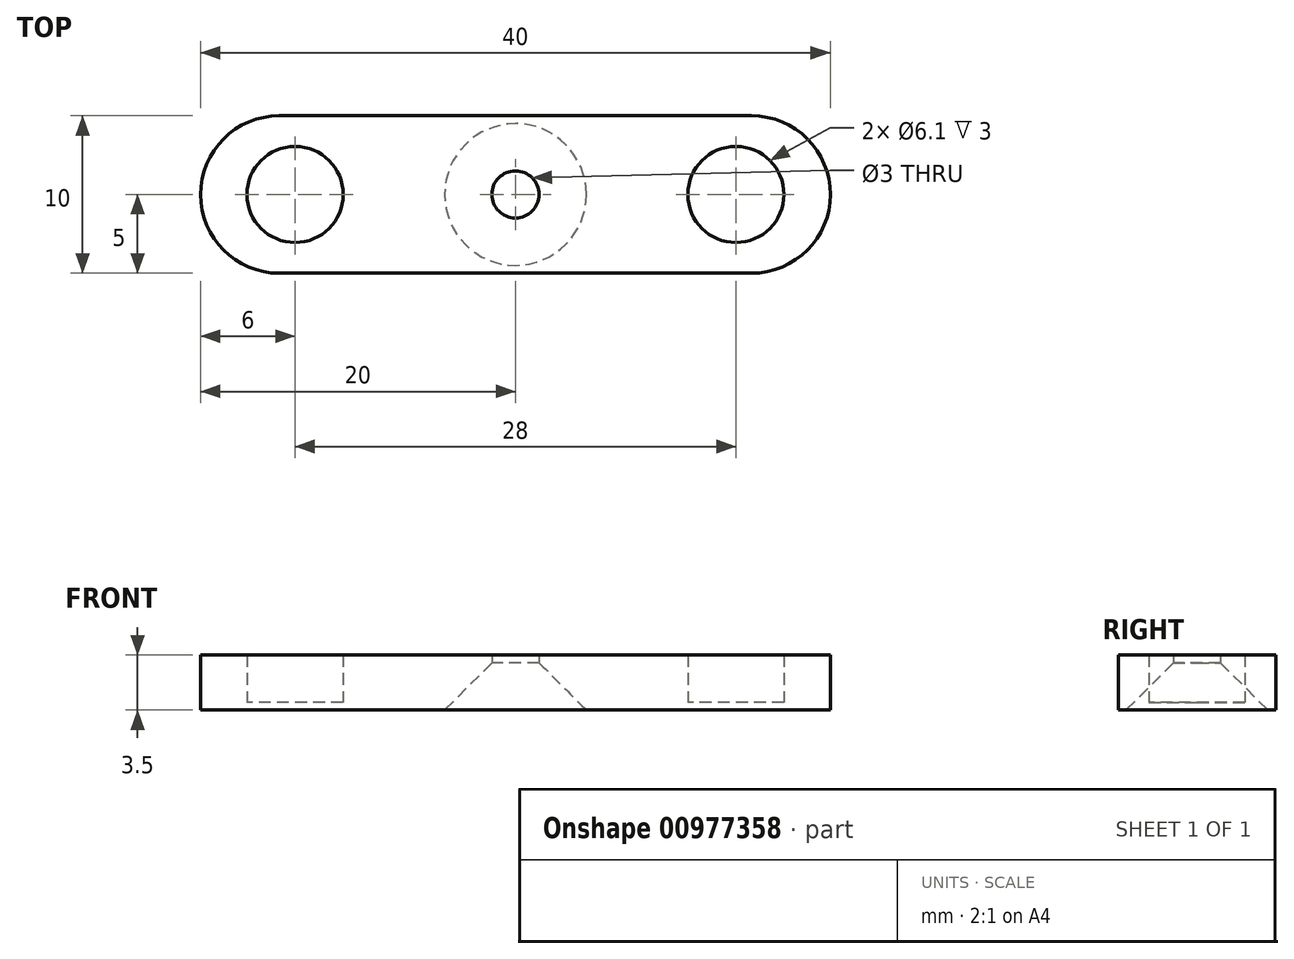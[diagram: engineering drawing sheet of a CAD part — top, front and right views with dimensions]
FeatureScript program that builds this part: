
annotation { "Feature Type Name" : "Feature", "Feature Type Description" : "" }
export const myFeature = defineFeature(function(context is Context, id is Id, definition is map)
    precondition{}
    {
        {
            var Q0;
            Q0=qCreatedBy(makeId("Top.planeOp"),FACE);
            var sketch = newSketch(context, id + "F0", { "sketchPlane" : qUnion([Q0])});
            skLineSegment(sketch, "E0.bottom", {"start": v(20, 5) * mm, "end": v(-20, 5) * mm});
            skLineSegment(sketch, "E0.top", {"start": v(20, -5) * mm, "end": v(-20, -5) * mm});
            skLineSegment(sketch, "E0.left", {"start": v(20, 5) * mm, "end": v(20, -5) * mm});
            skLineSegment(sketch, "E0.right", {"start": v(-20, 5) * mm, "end": v(-20, -5) * mm});
            skPoint(sketch, "E0.middle", {"position": v(0, 0) * mm});
            skCircle(sketch, "E1", {"center": v(-14, 0) * mm, "radius": 3.05 * mm});
            skCircle(sketch, "E2", {"center": v(14, 0) * mm, "radius": 3.05 * mm});
            skCircle(sketch, "E3", {"center": v(0, 0) * mm, "radius": 1.5 * mm});
            skSolve(sketch);
        }
        {
            var Q0;
            Q0=makeQuery(id+"F0.imprint","IMPRINT",FACE,{"disambiguationData":[TD([[makeQuery(id+"F0.imprint","IMPRINT",EDGE,{"derivedFrom":sQuery(id+"F0.wireOp",EDGE,"E0.bottom")}),1.0]])]});
            var Q1;
            Q1=makeQuery(id+"F0.imprint","IMPRINT",FACE,{"disambiguationData":[TD([[makeQuery(id+"F0.imprint","IMPRINT",EDGE,{"derivedFrom":sQuery(id+"F0.wireOp",EDGE,"E1")}),1.0]])]});
            var Q2;
            Q2=makeQuery(id+"F0.imprint","IMPRINT",FACE,{"disambiguationData":[TD([[makeQuery(id+"F0.imprint","IMPRINT",EDGE,{"derivedFrom":sQuery(id+"F0.wireOp",EDGE,"E2")}),1.0]])]});
            extrude(context, id + "F1", {"entities" : qUnion([Q0, Q1, Q2]), "depth" : 0.5 * mm, "offsetDistance" : 25 * mm});
        }
        {
            var Q0;
            Q0=makeQuery(id+"F0.imprint","IMPRINT",FACE,{"disambiguationData":[TD([[makeQuery(id+"F0.imprint","IMPRINT",EDGE,{"derivedFrom":sQuery(id+"F0.wireOp",EDGE,"E0.bottom")}),1.0]])]});
            extrude(context, id + "F2", {"entities" : qUnion([Q0]), "operationType" : NewBodyOperationType.ADD, "depth" : 3.5 * mm, "offsetDistance" : 25 * mm});
        }
        {
            var Q0;
            {var subQ0=sQuery(id+"F0.wireOp",EDGE,"E0.left");var subQ1=sQuery(id+"F0.wireOp",EDGE,"E0.bottom");Q0=makeQuery(id+"F2.boolean.opBoolean","MERGE",EDGE,{"derivedFrom":[makeQuery(id+"F1.opExtrude","SWEPT_EDGE",EDGE,{"disambiguationData":[OSD([subQ1,subQ0])]}),makeQuery(id+"F2.opExtrude","SWEPT_EDGE",EDGE,{"disambiguationData":[OSD([subQ1,subQ0])]})]});}
            var Q1;
            {var subQ0=sQuery(id+"F0.wireOp",EDGE,"E0.left");var subQ1=sQuery(id+"F0.wireOp",EDGE,"E0.top");Q1=makeQuery(id+"F2.boolean.opBoolean","MERGE",EDGE,{"derivedFrom":[makeQuery(id+"F1.opExtrude","SWEPT_EDGE",EDGE,{"disambiguationData":[OSD([subQ1,subQ0])]}),makeQuery(id+"F2.opExtrude","SWEPT_EDGE",EDGE,{"disambiguationData":[OSD([subQ1,subQ0])]})]});}
            var Q2;
            {var subQ0=sQuery(id+"F0.wireOp",EDGE,"E0.right");var subQ1=sQuery(id+"F0.wireOp",EDGE,"E0.top");Q2=makeQuery(id+"F2.boolean.opBoolean","MERGE",EDGE,{"derivedFrom":[makeQuery(id+"F1.opExtrude","SWEPT_EDGE",EDGE,{"disambiguationData":[OSD([subQ1,subQ0])]}),makeQuery(id+"F2.opExtrude","SWEPT_EDGE",EDGE,{"disambiguationData":[OSD([subQ1,subQ0])]})]});}
            var Q3;
            {var subQ0=sQuery(id+"F0.wireOp",EDGE,"E0.right");var subQ1=sQuery(id+"F0.wireOp",EDGE,"E0.bottom");Q3=makeQuery(id+"F2.boolean.opBoolean","MERGE",EDGE,{"derivedFrom":[makeQuery(id+"F1.opExtrude","SWEPT_EDGE",EDGE,{"disambiguationData":[OSD([subQ1,subQ0])]}),makeQuery(id+"F2.opExtrude","SWEPT_EDGE",EDGE,{"disambiguationData":[OSD([subQ1,subQ0])]})]});}
            fillet(context, id + "F3", {"entities" : qUnion([Q0, Q1, Q2, Q3]), "radius" : 5 * mm, "tangentPropagation" : true, "allowEdgeOverflow" : false});
        }
        {
            var Q0;
            Q0=makeQuery(id+"F1.opExtrude","CAP_EDGE",EDGE,{"disambiguationData":[OSD([sQuery(id+"F0.wireOp",EDGE,"E3")])],"isStart":true});
            chamfer(context, id + "F4", {"entities" : qUnion([Q0]), "width" : 3 * mm, "tangentPropagation" : true});
        }
    });
